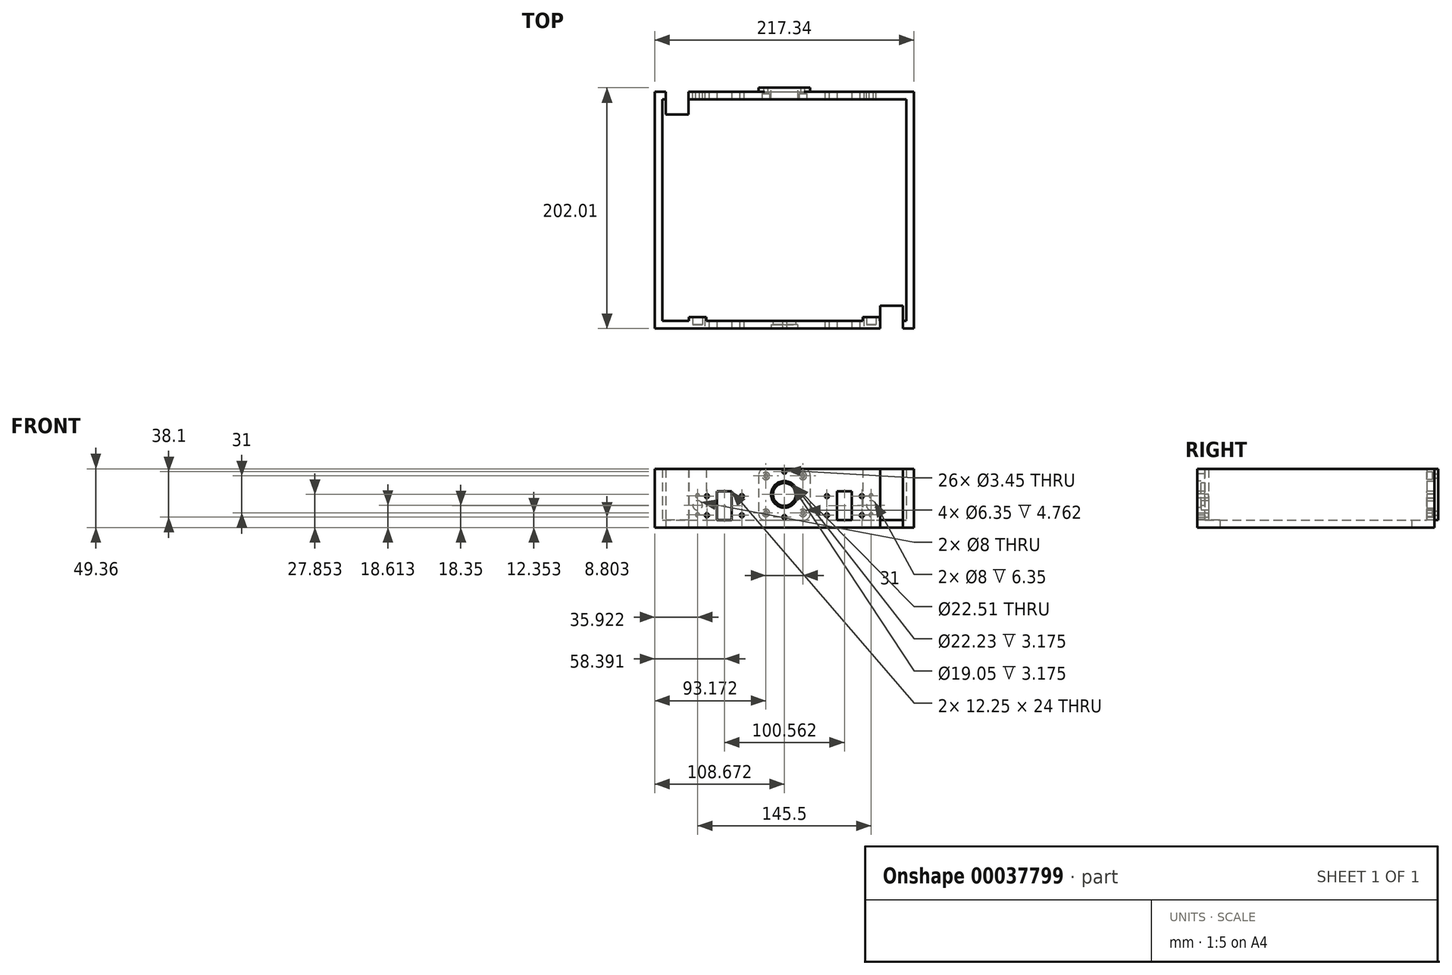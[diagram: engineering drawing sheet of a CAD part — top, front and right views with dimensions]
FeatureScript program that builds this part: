
annotation { "Feature Type Name" : "Feature", "Feature Type Description" : "" }
export const myFeature = defineFeature(function(context is Context, id is Id, definition is map)
    precondition{}
    {
        {
            var Q0;
            Q0=qCreatedBy(makeId("Top.planeOp"),FACE);
            var sketch = newSketch(context, id + "F0", { "sketchPlane" : qUnion([Q0])});
            skLineSegment(sketch, "E0.bottom", {"start": v(0, 0) * mm, "end": v(217.34, 0) * mm});
            skLineSegment(sketch, "E0.top", {"start": v(0, -198.6) * mm, "end": v(217.34, -198.6) * mm});
            skLineSegment(sketch, "E0.left", {"start": v(0, 0) * mm, "end": v(0, -198.6) * mm});
            skLineSegment(sketch, "E0.right", {"start": v(217.34, 0) * mm, "end": v(217.34, -198.6) * mm});
            skSolve(sketch);
        }
        {
            var Q0;
            Q0=qSketchRegion(id+"F0",true);
            extrude(context, id + "F1", {"entities" : qUnion([Q0]), "depth" : 6.35 * mm});
        }
        {
            var Q0;
            Q0=makeQuery(id+"F1.opExtrude","CAP_FACE",FACE,{"disambiguationData":[OSD([sQuery(id+"F0.wireOp",EDGE,"E0.bottom"),sQuery(id+"F0.wireOp",EDGE,"E0.top"),sQuery(id+"F0.wireOp",EDGE,"E0.left"),sQuery(id+"F0.wireOp",EDGE,"E0.right"),sQuery(id+"F0.wireOp",EDGE,"0dc974a7-bb18-41b5-bac5-504b73813e93.bottom"),sQuery(id+"F0.wireOp",EDGE,"0dc974a7-bb18-41b5-bac5-504b73813e93.top"),sQuery(id+"F0.wireOp",EDGE,"0dc974a7-bb18-41b5-bac5-504b73813e93.left"),sQuery(id+"F0.wireOp",EDGE,"0dc974a7-bb18-41b5-bac5-504b73813e93.right"),sQuery(id+"F0.wireOp",EDGE,"a5e80c1d-3b18-4d21-875b-c5de23a3e49a.bottom"),sQuery(id+"F0.wireOp",EDGE,"a5e80c1d-3b18-4d21-875b-c5de23a3e49a.top"),sQuery(id+"F0.wireOp",EDGE,"a5e80c1d-3b18-4d21-875b-c5de23a3e49a.left"),sQuery(id+"F0.wireOp",EDGE,"a5e80c1d-3b18-4d21-875b-c5de23a3e49a.right"),sQuery(id+"F0.wireOp",EDGE,"8457256c-00b8-499a-bc30-1e1db44eeaf8.bottom"),sQuery(id+"F0.wireOp",EDGE,"8457256c-00b8-499a-bc30-1e1db44eeaf8.top"),sQuery(id+"F0.wireOp",EDGE,"8457256c-00b8-499a-bc30-1e1db44eeaf8.left"),sQuery(id+"F0.wireOp",EDGE,"8457256c-00b8-499a-bc30-1e1db44eeaf8.right"),sQuery(id+"F0.wireOp",EDGE,"1e8e9123-19b8-4ca4-a39b-8ebd56aa32be.bottom"),sQuery(id+"F0.wireOp",EDGE,"1e8e9123-19b8-4ca4-a39b-8ebd56aa32be.top"),sQuery(id+"F0.wireOp",EDGE,"1e8e9123-19b8-4ca4-a39b-8ebd56aa32be.left"),sQuery(id+"F0.wireOp",EDGE,"1e8e9123-19b8-4ca4-a39b-8ebd56aa32be.right"),sQuery(id+"F0.wireOp",EDGE,"c83f6c4d-6001-42a2-b69e-674a973808aa"),sQuery(id+"F0.wireOp",EDGE,"e059eaf3-c2a5-4160-8620-3459575baeff"),sQuery(id+"F0.wireOp",EDGE,"809cc3f0-17a7-4fbb-9f5a-5ee0d5a7ab00"),sQuery(id+"F0.wireOp",EDGE,"55fcec49-ac1f-4b6a-b4a8-b54db98f405a"),sQuery(id+"F0.wireOp",EDGE,"92878443-5987-4af0-ba37-ad07abb5a4d0"),sQuery(id+"F0.wireOp",EDGE,"2dc40d28-0d46-4c28-b739-26dd6c8f13d1"),sQuery(id+"F0.wireOp",EDGE,"7ae3ad1e-5f8b-4898-8e08-88fdf3906e76"),sQuery(id+"F0.wireOp",EDGE,"b5510cef-4e8d-4c4e-ba46-f795b444ae90")])],"isStart":false});
            var sketch = newSketch(context, id + "F2", { "sketchPlane" : qUnion([Q0])});
            skLineSegment(sketch, "E1", {"start": v(0, -99.3) * mm, "end": v(217.34, -99.3) * mm, "construction": true});
            skLineSegment(sketch, "E2.rect.bottom", {"start": v(0, -198.6) * mm, "end": v(217.34, -198.6) * mm});
            skLineSegment(sketch, "E2.rect.top", {"start": v(0, 0) * mm, "end": v(217.34, 0) * mm});
            skLineSegment(sketch, "E2.rect.left", {"start": v(0, -198.6) * mm, "end": v(0, 0) * mm});
            skLineSegment(sketch, "E2.rect.right", {"start": v(217.34, -198.6) * mm, "end": v(217.34, 0) * mm});
            skPoint(sketch, "E2.rect.middle", {"position": v(108.67, -99.3) * mm});
            skLineSegment(sketch, "E3.rect.bottom", {"start": v(6.35, -192.25) * mm, "end": v(211, -192.25) * mm});
            skLineSegment(sketch, "E3.rect.top", {"start": v(6.35, -6.35) * mm, "end": v(211, -6.35) * mm});
            skLineSegment(sketch, "E3.rect.left", {"start": v(6.35, -192.25) * mm, "end": v(6.35, -6.35) * mm});
            skLineSegment(sketch, "E3.rect.right", {"start": v(211, -192.25) * mm, "end": v(211, -6.35) * mm});
            skLineSegment(sketch, "E4", {"start": v(108.67, -192.25) * mm, "end": v(108.67, -198.6) * mm, "construction": true});
            skLineSegment(sketch, "E5", {"start": v(6.35, -192.25) * mm, "end": v(0, -192.25) * mm, "construction": true});
            skSolve(sketch);
        }
        {
            var Q0;
            Q0=qSketchRegion(id+"F2",true);
            var Q1;
            {var subQ3=makeQuery(id+"F1.opExtrude","CAP_EDGE",EDGE,{"disambiguationData":[OSD([sQuery(id+"F0.wireOp",EDGE,"45716fd8-2d04-414a-a1f4-580c9c1d9f1b")])],"isStart":false});Q1=makeQuery(id+"F2.imprint","IMPRINT",FACE,{"disambiguationData":[TD([[makeQuery(id+"F2.imprint","IMPRINT",EDGE,{"derivedFrom":subQ3}),-1.0]])]});}
            var Q2;
            {var subQ3=makeQuery(id+"F1.opExtrude","CAP_EDGE",EDGE,{"disambiguationData":[OSD([sQuery(id+"F0.wireOp",EDGE,"0e2d7a09-d9f5-4aca-b445-2d3464167acf")])],"isStart":false});Q2=makeQuery(id+"F2.imprint","IMPRINT",FACE,{"disambiguationData":[TD([[makeQuery(id+"F2.imprint","IMPRINT",EDGE,{"derivedFrom":subQ3}),1.0]])]});}
            extrude(context, id + "F3", {"entities" : qUnion([Q0, Q1, Q2]), "operationType" : NewBodyOperationType.ADD, "depth" : 43 * mm});
        }
        {
            var Q0;
            Q0=makeQuery(id+"F3.boolean.opBoolean","MERGE",FACE,{"derivedFrom":[makeQuery(id+"F1.opExtrude","SWEPT_FACE",FACE,{"disambiguationData":[OSD([sQuery(id+"F0.wireOp",EDGE,"E0.bottom")])]}),makeQuery(id+"F3.opExtrude","SWEPT_FACE",FACE,{"disambiguationData":[OSD([sQuery(id+"F2.wireOp",EDGE,"E2.rect.top")])]})]});
            var sketch = newSketch(context, id + "F4", { "sketchPlane" : qUnion([Q0])});
            skLineSegment(sketch, "E6.rect.bottom", {"start": v(-93.17, 43.35) * mm, "end": v(-124.17, 43.35) * mm, "construction": true});
            skLineSegment(sketch, "E6.rect.top", {"start": v(-93.17, 12.35) * mm, "end": v(-124.17, 12.35) * mm, "construction": true});
            skLineSegment(sketch, "E6.rect.left", {"start": v(-93.17, 43.35) * mm, "end": v(-93.17, 12.35) * mm, "construction": true});
            skLineSegment(sketch, "E6.rect.right", {"start": v(-124.17, 43.35) * mm, "end": v(-124.17, 12.35) * mm, "construction": true});
            skPoint(sketch, "E6.rect.middle", {"position": v(-108.67, 27.85) * mm});
            skCircle(sketch, "E7", {"center": v(-124.17, 43.35) * mm, "radius": 1.73 * mm});
            skCircle(sketch, "E8", {"center": v(-93.17, 43.35) * mm, "radius": 1.73 * mm});
            skCircle(sketch, "E9", {"center": v(-124.17, 12.35) * mm, "radius": 1.73 * mm});
            skCircle(sketch, "E10", {"center": v(-108.67, 27.85) * mm, "radius": 11.25 * mm});
            skCircle(sketch, "E11", {"center": v(-93.17, 12.35) * mm, "radius": 1.73 * mm});
            skLineSegment(sketch, "E12", {"start": v(-35.92, 18.61) * mm, "end": v(-35.92, 6.35) * mm, "construction": true});
            skCircle(sketch, "E13", {"center": v(-181.42, 18.61) * mm, "radius": 4 * mm});
            skCircle(sketch, "E14", {"center": v(-35.92, 18.61) * mm, "radius": 4 * mm});
            skLineSegment(sketch, "E15", {"start": v(-35.92, 18.61) * mm, "end": v(-6.35, 18.61) * mm, "construction": true});
            skLineSegment(sketch, "E16", {"start": v(-35.92, 18.61) * mm, "end": v(-181.42, 18.61) * mm, "construction": true});
            skLineSegment(sketch, "E17", {"start": v(-108.67, 27.85) * mm, "end": v(-108.67, 6.35) * mm, "construction": true});
            skPoint(sketch, "E18", {"position": v(-108.67, 18.61) * mm});
            skSolve(sketch);
        }
        {
            var Q0;
            Q0=qSketchRegion(id+"F4",true);
            var Q1;
            Q1=makeQuery(id+"F3.opExtrude","SWEPT_FACE",FACE,{"disambiguationData":[OSD([sQuery(id+"F2.wireOp",EDGE,"E3.rect.top")])]});
            extrude(context, id + "F5", {"entities" : qUnion([Q0]), "operationType" : NewBodyOperationType.REMOVE, "endBound" : BoundingType.UP_TO_SURFACE, "oppositeDirection" : true, "endBoundEntityFace" : qUnion([Q1]), "depth" : 25.4 * mm});
        }
        {
            var Q0;
            Q0=qSketchRegion(id+"F4",true);
            var Q1;
            Q1=makeQuery(id+"F3.opExtrude","SWEPT_FACE",FACE,{"disambiguationData":[OSD([sQuery(id+"F2.wireOp",EDGE,"E3.rect.top")])]});
            extrude(context, id + "F6", {"entities" : qUnion([Q0]), "operationType" : NewBodyOperationType.REMOVE, "endBound" : BoundingType.UP_TO_SURFACE, "oppositeDirection" : true, "endBoundEntityFace" : qUnion([Q1]), "depth" : 25.4 * mm});
        }
        {
            var Q0;
            Q0=makeQuery(id+"F3.boolean.opBoolean","MERGE",FACE,{"derivedFrom":[makeQuery(id+"F1.opExtrude","SWEPT_FACE",FACE,{"disambiguationData":[OSD([sQuery(id+"F0.wireOp",EDGE,"E0.top")])]}),makeQuery(id+"F3.opExtrude","SWEPT_FACE",FACE,{"disambiguationData":[OSD([sQuery(id+"F2.wireOp",EDGE,"E2.rect.bottom")])]})]});
            var sketch = newSketch(context, id + "F7", { "sketchPlane" : qUnion([Q0])});
            skCircle(sketch, "E19", {"center": v(108.67, 27.85) * mm, "radius": 11.11 * mm});
            skSolve(sketch);
        }
        {
            var Q0;
            Q0 = qSketchRegion(id + "F7", true);
            extrude(context, id + "F8", {"entities" : qUnion([Q0]), "operationType" : NewBodyOperationType.REMOVE, "oppositeDirection" : true, "depth" : 3.17 * mm});
        }
        {
            var Q0;
            Q0=makeQuery(id+"F8.boolean.opBoolean","COPY",FACE,{"derivedFrom":makeQuery(id+"F8.opExtrude","CAP_FACE",FACE,{"disambiguationData":[OSD([sQuery(id+"F7.wireOp",EDGE,"E19")])],"isStart":false})});
            var sketch = newSketch(context, id + "F9", { "sketchPlane" : qUnion([Q0])});
            skCircle(sketch, "E20", {"center": v(108.67, 27.85) * mm, "radius": 9.53 * mm});
            skSolve(sketch);
        }
        {
            var Q0;
            Q0 = qSketchRegion(id + "F9", true);
            var Q1;
            Q1=makeQuery(id+"F3.opExtrude","SWEPT_FACE",FACE,{"disambiguationData":[OSD([sQuery(id+"F2.wireOp",EDGE,"E3.rect.bottom")])]});
            extrude(context, id + "F10", {"entities" : qUnion([Q0]), "operationType" : NewBodyOperationType.REMOVE, "endBound" : BoundingType.UP_TO_SURFACE, "oppositeDirection" : true, "endBoundEntityFace" : qUnion([Q1]), "depth" : 25.4 * mm});
        }
        {
            var Q0;
            Q0=makeQuery(id+"FYWy5oApQTNVcxj_1.boolean.opBoolean","MERGE",FACE,{"derivedFrom":[makeQuery(id+"F3.boolean.opBoolean","MERGE",FACE,{"derivedFrom":[makeQuery(id+"F1.opExtrude","SWEPT_FACE",FACE,{"disambiguationData":[OSD([sQuery(id+"F0.wireOp",EDGE,"E0.top")])]}),makeQuery(id+"F3.opExtrude","SWEPT_FACE",FACE,{"disambiguationData":[OSD([sQuery(id+"F2.wireOp",EDGE,"E2.rect.bottom")])]})]}),makeQuery(id+"FYWy5oApQTNVcxj_1.opExtrude","SWEPT_FACE",FACE,{"disambiguationData":[OSD([sQuery(id+"F2eOpnR5XSKowKk_1.wireOp",EDGE,"03125152-d2a7-4a82-b177-53cdc44c2ee3.left")])]})]});
            var sketch = newSketch(context, id + "F11", { "sketchPlane" : qUnion([Q0])});
            skLineSegment(sketch, "E21", {"start": v(108.67, 46.9) * mm, "end": v(108.67, 8.8) * mm, "construction": true});
            skPoint(sketch, "E22", {"position": v(108.67, 27.85) * mm});
            skCircle(sketch, "E23", {"center": v(108.67, 46.9) * mm, "radius": 1.73 * mm});
            skCircle(sketch, "E24", {"center": v(108.67, 8.8) * mm, "radius": 1.73 * mm});
            skSolve(sketch);
        }
        {
            var Q0;
            Q0 = qSketchRegion(id + "F11", true);
            var Q1;
            Q1=makeQuery(id+"F3.opExtrude","SWEPT_FACE",FACE,{"disambiguationData":[OSD([sQuery(id+"F2.wireOp",EDGE,"E3.rect.bottom")])]});
            extrude(context, id + "F12", {"entities" : qUnion([Q0]), "operationType" : NewBodyOperationType.REMOVE, "endBound" : BoundingType.UP_TO_SURFACE, "oppositeDirection" : true, "endBoundEntityFace" : qUnion([Q1]), "depth" : 25.4 * mm});
        }
        {
            var Q0;
            Q0=makeQuery(id+"F3.opExtrude","SWEPT_FACE",FACE,{"disambiguationData":[OSD([sQuery(id+"F2.wireOp",EDGE,"E3.rect.bottom")])]});
            var sketch = newSketch(context, id + "F13", { "sketchPlane" : qUnion([Q0])});
            skLineSegment(sketch, "E25.bottom", {"start": v(-28.75, 49.36) * mm, "end": v(-43.1, 49.36) * mm});
            skLineSegment(sketch, "E25.top", {"start": v(-28.75, 6.35) * mm, "end": v(-43.1, 6.35) * mm});
            skLineSegment(sketch, "E25.left", {"start": v(-43.1, 49.36) * mm, "end": v(-43.1, 6.35) * mm});
            skLineSegment(sketch, "E25.right", {"start": v(-28.75, 49.36) * mm, "end": v(-28.75, 6.35) * mm});
            skLineSegment(sketch, "E26.bottom", {"start": v(-174.25, 49.36) * mm, "end": v(-188.6, 49.36) * mm});
            skLineSegment(sketch, "E26.top", {"start": v(-174.25, 6.35) * mm, "end": v(-188.6, 6.35) * mm});
            skLineSegment(sketch, "E26.left", {"start": v(-174.25, 49.36) * mm, "end": v(-174.25, 6.35) * mm});
            skLineSegment(sketch, "E26.right", {"start": v(-188.6, 49.36) * mm, "end": v(-188.6, 6.35) * mm});
            skLineSegment(sketch, "E27", {"start": v(-35.92, 49.36) * mm, "end": v(-35.92, 18.61) * mm});
            skLineSegment(sketch, "E28", {"start": v(-181.42, 49.36) * mm, "end": v(-181.42, 18.61) * mm});
            skCircle(sketch, "E29", {"center": v(-181.42, 18.61) * mm, "radius": 4 * mm});
            skCircle(sketch, "E30", {"center": v(-35.92, 18.61) * mm, "radius": 4 * mm});
            skSolve(sketch);
        }
        {
            var Q0;
            Q0 = qSketchRegion(id + "F13", true);
            extrude(context, id + "F14", {"entities" : qUnion([Q0]), "operationType" : NewBodyOperationType.ADD, "depth" : 3.17 * mm});
        }
        {
            var Q0;
            Q0=makeQuery(id+"F14.boolean.opBoolean","SPLIT",FACE,{"disambiguationData":[TD([makeQuery(id+"F14.opExtrude","SWEPT_FACE",FACE,{"disambiguationData":[OSD([sQuery(id+"F13.wireOp",EDGE,"E29")])]})])],"derivedFrom":makeQuery(id+"F3.opExtrude","SWEPT_FACE",FACE,{"disambiguationData":[OSD([sQuery(id+"F2.wireOp",EDGE,"E3.rect.bottom")])]})});
            var Q1;
            Q1=makeQuery(id+"F14.boolean.opBoolean","SPLIT",FACE,{"disambiguationData":[TD([makeQuery(id+"F14.opExtrude","SWEPT_FACE",FACE,{"disambiguationData":[OSD([sQuery(id+"F13.wireOp",EDGE,"E30")])]})])],"derivedFrom":makeQuery(id+"F3.opExtrude","SWEPT_FACE",FACE,{"disambiguationData":[OSD([sQuery(id+"F2.wireOp",EDGE,"E3.rect.bottom")])]})});
            extrude(context, id + "F15", {"entities" : qUnion([Q0, Q1]), "operationType" : NewBodyOperationType.REMOVE, "oppositeDirection" : true, "depth" : 3.17 * mm});
        }
        {
            var Q0;
            Q0=makeQuery(id+"Fr43RmmgDeaCVq5_1.boolean.opBoolean","MERGE",FACE,{"derivedFrom":[makeQuery(id+"F3.boolean.opBoolean","MERGE",FACE,{"derivedFrom":[makeQuery(id+"F1.opExtrude","SWEPT_FACE",FACE,{"disambiguationData":[OSD([sQuery(id+"F0.wireOp",EDGE,"E0.bottom")])]}),makeQuery(id+"F3.opExtrude","SWEPT_FACE",FACE,{"disambiguationData":[OSD([sQuery(id+"F2.wireOp",EDGE,"E2.rect.top")])]})]}),makeQuery(id+"Fr43RmmgDeaCVq5_1.opExtrude","SWEPT_FACE",FACE,{"disambiguationData":[OSD([sQuery(id+"FCd6odW5DkVmG3E_1.wireOp",EDGE,"33830bfe-1f8d-4ee9-affb-1e3e39a7302c.left")])]})]});
            var sketch = newSketch(context, id + "F16", { "sketchPlane" : qUnion([Q0])});
            skLineSegment(sketch, "E31", {"start": v(-181.42, 10.64) * mm, "end": v(-181.42, 26.58) * mm, "construction": true});
            skLineSegment(sketch, "E32", {"start": v(-35.92, 26.58) * mm, "end": v(-35.92, 10.64) * mm, "construction": true});
            skCircle(sketch, "E33", {"center": v(-181.42, 10.64) * mm, "radius": 1.73 * mm});
            skCircle(sketch, "E34", {"center": v(-181.42, 26.58) * mm, "radius": 1.73 * mm});
            skCircle(sketch, "E35", {"center": v(-35.92, 10.64) * mm, "radius": 1.73 * mm});
            skCircle(sketch, "E36", {"center": v(-35.92, 26.58) * mm, "radius": 1.73 * mm});
            skCircle(sketch, "E37", {"center": v(-181.42, 10.64) * mm, "radius": 3.97 * mm, "construction": true});
            skPoint(sketch, "E38", {"position": v(-35.92, 18.61) * mm});
            skPoint(sketch, "E39", {"position": v(-181.42, 18.61) * mm});
            skSolve(sketch);
        }
        {
            var Q0;
            Q0 = qSketchRegion(id + "F16", true);
            var Q1;
            Q1=makeQuery(id+"F3.opExtrude","SWEPT_FACE",FACE,{"disambiguationData":[OSD([sQuery(id+"F2.wireOp",EDGE,"E3.rect.top")])]});
            extrude(context, id + "F17", {"entities" : qUnion([Q0]), "operationType" : NewBodyOperationType.REMOVE, "endBound" : BoundingType.UP_TO_SURFACE, "oppositeDirection" : true, "endBoundEntityFace" : qUnion([Q1]), "depth" : 25.4 * mm});
        }
        {
            var Q0;
            Q0=makeQuery(id+"FYWy5oApQTNVcxj_1.boolean.opBoolean","MERGE",FACE,{"derivedFrom":[makeQuery(id+"F3.boolean.opBoolean","MERGE",FACE,{"derivedFrom":[makeQuery(id+"F1.opExtrude","SWEPT_FACE",FACE,{"disambiguationData":[OSD([sQuery(id+"F0.wireOp",EDGE,"E0.top")])]}),makeQuery(id+"F3.opExtrude","SWEPT_FACE",FACE,{"disambiguationData":[OSD([sQuery(id+"F2.wireOp",EDGE,"E2.rect.bottom")])]})]}),makeQuery(id+"FYWy5oApQTNVcxj_1.opExtrude","SWEPT_FACE",FACE,{"disambiguationData":[OSD([sQuery(id+"F2eOpnR5XSKowKk_1.wireOp",EDGE,"03125152-d2a7-4a82-b177-53cdc44c2ee3.left")])]})]});
            var sketch = newSketch(context, id + "F18", { "sketchPlane" : qUnion([Q0])});
            skLineSegment(sketch, "E40.rect.left", {"start": v(165.08, 30.35) * mm, "end": v(165.08, 6.35) * mm});
            skLineSegment(sketch, "E40.rect.right", {"start": v(152.83, 30.35) * mm, "end": v(152.83, 6.35) * mm});
            skLineSegment(sketch, "E41.rect.bottom", {"start": v(173.6, 26.38) * mm, "end": v(144.3, 26.38) * mm, "construction": true});
            skLineSegment(sketch, "E41.rect.top", {"start": v(173.6, 10.32) * mm, "end": v(144.3, 10.32) * mm, "construction": true});
            skLineSegment(sketch, "E42", {"start": v(158.95, 18.35) * mm, "end": v(217.34, 18.35) * mm, "construction": true});
            skLineSegment(sketch, "E41.rect.left", {"start": v(173.6, 26.38) * mm, "end": v(173.6, 10.32) * mm, "construction": true});
            skLineSegment(sketch, "E41.rect.right", {"start": v(144.3, 26.38) * mm, "end": v(144.3, 10.32) * mm, "construction": true});
            skLineSegment(sketch, "E40.rect.bottom", {"start": v(165.08, 30.35) * mm, "end": v(152.83, 30.35) * mm});
            skLineSegment(sketch, "E40.rect.top", {"start": v(165.08, 6.35) * mm, "end": v(152.83, 6.35) * mm});
            skCircle(sketch, "E43", {"center": v(173.6, 26.38) * mm, "radius": 1.73 * mm});
            skCircle(sketch, "E44", {"center": v(173.6, 10.32) * mm, "radius": 1.73 * mm});
            skCircle(sketch, "E45", {"center": v(144.3, 26.38) * mm, "radius": 1.73 * mm});
            skCircle(sketch, "E46", {"center": v(144.3, 10.32) * mm, "radius": 1.73 * mm});
            skLineSegment(sketch, "E47", {"start": v(158.95, 18.35) * mm, "end": v(58.4, 18.35) * mm, "construction": true});
            skLineSegment(sketch, "E48", {"start": v(58.4, 18.35) * mm, "end": v(0, 18.35) * mm, "construction": true});
            skLineSegment(sketch, "E49.rect.bottom", {"start": v(52.26, 30.35) * mm, "end": v(64.52, 30.35) * mm});
            skLineSegment(sketch, "E49.rect.top", {"start": v(52.26, 6.35) * mm, "end": v(64.52, 6.35) * mm});
            skLineSegment(sketch, "E49.rect.left", {"start": v(52.26, 30.35) * mm, "end": v(52.26, 6.35) * mm});
            skLineSegment(sketch, "E49.rect.right", {"start": v(64.52, 30.35) * mm, "end": v(64.52, 6.35) * mm});
            skPoint(sketch, "E49.rect.middle", {"position": v(58.4, 18.35) * mm});
            skLineSegment(sketch, "E50.rect.bottom", {"start": v(43.75, 26.38) * mm, "end": v(73.03, 26.38) * mm, "construction": true});
            skLineSegment(sketch, "E50.rect.top", {"start": v(43.75, 10.32) * mm, "end": v(73.03, 10.32) * mm, "construction": true});
            skLineSegment(sketch, "E50.rect.left", {"start": v(43.75, 26.38) * mm, "end": v(43.75, 10.32) * mm, "construction": true});
            skLineSegment(sketch, "E50.rect.right", {"start": v(73.03, 26.38) * mm, "end": v(73.03, 10.32) * mm, "construction": true});
            skCircle(sketch, "E51", {"center": v(43.75, 26.38) * mm, "radius": 1.73 * mm});
            skCircle(sketch, "E52", {"center": v(73.03, 26.38) * mm, "radius": 1.73 * mm});
            skCircle(sketch, "E53", {"center": v(73.03, 10.32) * mm, "radius": 1.73 * mm});
            skCircle(sketch, "E54", {"center": v(43.75, 10.32) * mm, "radius": 1.73 * mm});
            skSolve(sketch);
        }
        {
            var Q0;
            Q0 = qSketchRegion(id + "F18", true);
            var Q1;
            Q1=makeQuery(id+"F3.boolean.opBoolean","MERGE",FACE,{"derivedFrom":[makeQuery(id+"F1.opExtrude","SWEPT_FACE",FACE,{"disambiguationData":[OSD([sQuery(id+"F0.wireOp",EDGE,"E0.bottom")])]}),makeQuery(id+"F3.opExtrude","SWEPT_FACE",FACE,{"disambiguationData":[OSD([sQuery(id+"F2.wireOp",EDGE,"E2.rect.top")])]})]});
            extrude(context, id + "F19", {"entities" : qUnion([Q0]), "operationType" : NewBodyOperationType.REMOVE, "endBound" : BoundingType.UP_TO_SURFACE, "oppositeDirection" : true, "endBoundEntityFace" : qUnion([Q1]), "depth" : 25.4 * mm});
        }
        {
            var Q0;
            Q0=makeQuery(id+"FxyTKgyFLJldC1U_1.boolean.opBoolean","MERGE",FACE,{"derivedFrom":[makeQuery(id+"F3.opExtrude","SWEPT_FACE",FACE,{"disambiguationData":[OSD([sQuery(id+"F2.wireOp",EDGE,"E3.rect.top")])]}),makeQuery(id+"FxyTKgyFLJldC1U_1.opExtrude","SWEPT_FACE",FACE,{"disambiguationData":[OSD([sQuery(id+"FN4gN3kQJJen3jx_1.wireOp",EDGE,"bbf2ca95-2885-4b1a-8bcf-762a3477a2aa")])]})]});
            var sketch = newSketch(context, id + "F20", { "sketchPlane" : qUnion([Q0])});
            skCircle(sketch, "E55", {"center": v(93.17, 43.35) * mm, "radius": 3.18 * mm});
            skCircle(sketch, "E56", {"center": v(124.17, 43.35) * mm, "radius": 3.18 * mm});
            skCircle(sketch, "E57", {"center": v(124.17, 12.35) * mm, "radius": 3.18 * mm});
            skCircle(sketch, "E58", {"center": v(93.17, 12.35) * mm, "radius": 3.18 * mm});
            skSolve(sketch);
        }
        {
            var Q0;
            Q0 = qSketchRegion(id + "F20", true);
            extrude(context, id + "F21", {"entities" : qUnion([Q0]), "operationType" : NewBodyOperationType.REMOVE, "oppositeDirection" : true, "depth" : 4.76 * mm});
        }
        {
            var Q0;
            Q0=makeQuery(id+"F3.boolean.opBoolean","MERGE",FACE,{"derivedFrom":[makeQuery(id+"F1.opExtrude","SWEPT_FACE",FACE,{"disambiguationData":[OSD([sQuery(id+"F0.wireOp",EDGE,"E0.bottom")])]}),makeQuery(id+"F3.opExtrude","SWEPT_FACE",FACE,{"disambiguationData":[OSD([sQuery(id+"F2.wireOp",EDGE,"E2.rect.top")])]})]});
            var sketch = newSketch(context, id + "F22", { "sketchPlane" : qUnion([Q0])});
            skLineSegment(sketch, "E59.rect.bottom", {"start": v(-87.17, 49.36) * mm, "end": v(-130.17, 49.36) * mm});
            skLineSegment(sketch, "E59.rect.top", {"start": v(-87.17, 6.35) * mm, "end": v(-130.17, 6.35) * mm});
            skLineSegment(sketch, "E59.rect.left", {"start": v(-87.17, 49.36) * mm, "end": v(-87.17, 6.35) * mm});
            skLineSegment(sketch, "E59.rect.right", {"start": v(-130.17, 49.36) * mm, "end": v(-130.17, 6.35) * mm});
            skPoint(sketch, "E59.rect.middle", {"position": v(-108.67, 27.85) * mm});
            skCircle(sketch, "E60", {"center": v(-108.67, 27.85) * mm, "radius": 11.25 * mm});
            skSolve(sketch);
        }
        {
            var Q0;
            Q0=makeQuery(id+"F22.imprint","IMPRINT",FACE,{"disambiguationData":[TD([[makeQuery(id+"F22.imprint","IMPRINT",EDGE,{"derivedFrom":sQuery(id+"F22.wireOp",EDGE,"E59.rect.bottom")}),1.0]])]});
            extrude(context, id + "F23", {"entities" : qUnion([Q0]), "operationType" : NewBodyOperationType.ADD, "depth" : 3.41 * mm});
        }
        {
            var Q0;
            Q0=makeQuery(id+"F23.opExtrude","SWEPT_EDGE",EDGE,{"disambiguationData":[OSD([sQuery(id+"F2.wireOp",EDGE,"E2.rect.top"),sQuery(id+"F22.wireOp",EDGE,"E59.rect.bottom"),sQuery(id+"F22.wireOp",EDGE,"E59.rect.left")])]});
            var Q1;
            Q1=makeQuery(id+"F23.opExtrude","SWEPT_EDGE",EDGE,{"disambiguationData":[OSD([sQuery(id+"F2.wireOp",EDGE,"E2.rect.top"),sQuery(id+"F22.wireOp",EDGE,"E59.rect.bottom"),sQuery(id+"F22.wireOp",EDGE,"E59.rect.right")])]});
            var Q2;
            Q2=makeQuery(id+"F23.opExtrude","SWEPT_EDGE",EDGE,{"disambiguationData":[OSD([sQuery(id+"F22.wireOp",EDGE,"E59.rect.top"),sQuery(id+"F22.wireOp",EDGE,"E59.rect.left")])]});
            var Q3;
            Q3=makeQuery(id+"F23.opExtrude","SWEPT_EDGE",EDGE,{"disambiguationData":[OSD([sQuery(id+"F22.wireOp",EDGE,"E59.rect.top"),sQuery(id+"F22.wireOp",EDGE,"E59.rect.right")])]});
            fillet(context, id + "F24", {"entities" : qUnion([Q0, Q1, Q2, Q3]), "radius" : 5.08 * mm, "tangentPropagation" : true, "allowEdgeOverflow" : false});
        }
        {
            var Q0;
            Q0=makeQuery(id+"F1.opExtrude","CAP_FACE",FACE,{"disambiguationData":[OSD([sQuery(id+"F0.wireOp",EDGE,"E0.bottom"),sQuery(id+"F0.wireOp",EDGE,"E0.top"),sQuery(id+"F0.wireOp",EDGE,"E0.left"),sQuery(id+"F0.wireOp",EDGE,"E0.right")])],"isStart":true});
            var sketch = newSketch(context, id + "F25", { "sketchPlane" : qUnion([Q0])});
            skLineSegment(sketch, "E61", {"start": v(0, 99.3) * mm, "end": v(217.34, 99.3) * mm, "construction": true});
            skLineSegment(sketch, "E62", {"start": v(18.9, 9.52) * mm, "end": v(198.45, 189.08) * mm, "construction": true});
            skPoint(sketch, "E63", {"position": v(108.67, 99.3) * mm});
            skLineSegment(sketch, "E64.rect.bottom", {"start": v(188.92, 198.6) * mm, "end": v(207.97, 198.6) * mm});
            skLineSegment(sketch, "E64.rect.top", {"start": v(188.92, 179.55) * mm, "end": v(207.97, 179.55) * mm});
            skLineSegment(sketch, "E64.rect.left", {"start": v(188.92, 198.6) * mm, "end": v(188.92, 179.55) * mm});
            skLineSegment(sketch, "E64.rect.right", {"start": v(207.97, 198.6) * mm, "end": v(207.97, 179.55) * mm});
            skPoint(sketch, "E64.rect.middle", {"position": v(198.45, 189.08) * mm});
            skLineSegment(sketch, "E65.rect.bottom", {"start": v(9.37, 0) * mm, "end": v(28.42, 0) * mm});
            skLineSegment(sketch, "E65.rect.top", {"start": v(9.37, 19.05) * mm, "end": v(28.42, 19.05) * mm});
            skLineSegment(sketch, "E65.rect.left", {"start": v(9.37, 0) * mm, "end": v(9.37, 19.05) * mm});
            skLineSegment(sketch, "E65.rect.right", {"start": v(28.42, 0) * mm, "end": v(28.42, 19.05) * mm});
            skPoint(sketch, "E65.rect.middle", {"position": v(18.9, 9.52) * mm});
            skSolve(sketch);
        }
        {
            var Q0;
            Q0 = qSketchRegion(id + "F25", true);
            var Q1;
            Q1=makeQuery(id+"F23.boolean.opBoolean","MERGE",FACE,{"derivedFrom":[makeQuery(id+"F14.boolean.opBoolean","MERGE",FACE,{"derivedFrom":[makeQuery(id+"F3.opExtrude","CAP_FACE",FACE,{"disambiguationData":[OSD([sQuery(id+"F2.wireOp",EDGE,"E2.rect.bottom"),sQuery(id+"F2.wireOp",EDGE,"E2.rect.top"),sQuery(id+"F2.wireOp",EDGE,"E2.rect.left"),sQuery(id+"F2.wireOp",EDGE,"E2.rect.right"),sQuery(id+"F2.wireOp",EDGE,"E3.rect.bottom"),sQuery(id+"F2.wireOp",EDGE,"E3.rect.top"),sQuery(id+"F2.wireOp",EDGE,"E3.rect.left"),sQuery(id+"F2.wireOp",EDGE,"E3.rect.right")])],"isStart":false}),makeQuery(id+"F14.opExtrude","SWEPT_FACE",FACE,{"disambiguationData":[OSD([sQuery(id+"F13.wireOp",EDGE,"E25.bottom")])]}),makeQuery(id+"F14.opExtrude","SWEPT_FACE",FACE,{"disambiguationData":[OSD([sQuery(id+"F13.wireOp",EDGE,"E26.bottom")])]})]}),makeQuery(id+"F23.opExtrude","SWEPT_FACE",FACE,{"disambiguationData":[OSD([sQuery(id+"F22.wireOp",EDGE,"E59.rect.bottom")])]})]});
            extrude(context, id + "F26", {"entities" : qUnion([Q0]), "operationType" : NewBodyOperationType.REMOVE, "endBound" : BoundingType.UP_TO_SURFACE, "oppositeDirection" : true, "endBoundEntityFace" : qUnion([Q1]), "depth" : 25.4 * mm});
        }
    });
